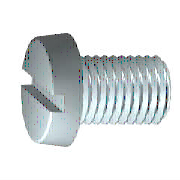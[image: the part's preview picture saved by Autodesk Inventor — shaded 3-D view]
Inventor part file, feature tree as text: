
AUTODESK INVENTOR PART (.ipt)
format: ipt  version: 2022 (Build 260153000, 153)  size: 187,392 bytes
history: native  units: mm (DEFAULTED — no unit token found)
features: sketch x2, other x1, extrude x1, plane x1
ambient origin geometry x7: Origin, YZ Plane, XZ Plane, X Axis, Y Axis, Z Axis, Center Point
bodies: Solid1 (feature_tree)
feature tree (5):
  other  "Базовый элемент"
  sketch  "Эскиз2"
  extrude  "Паз"  Depth=12.0mm
  plane  "Work Plane1"
  sketch  "Эскиз1"
